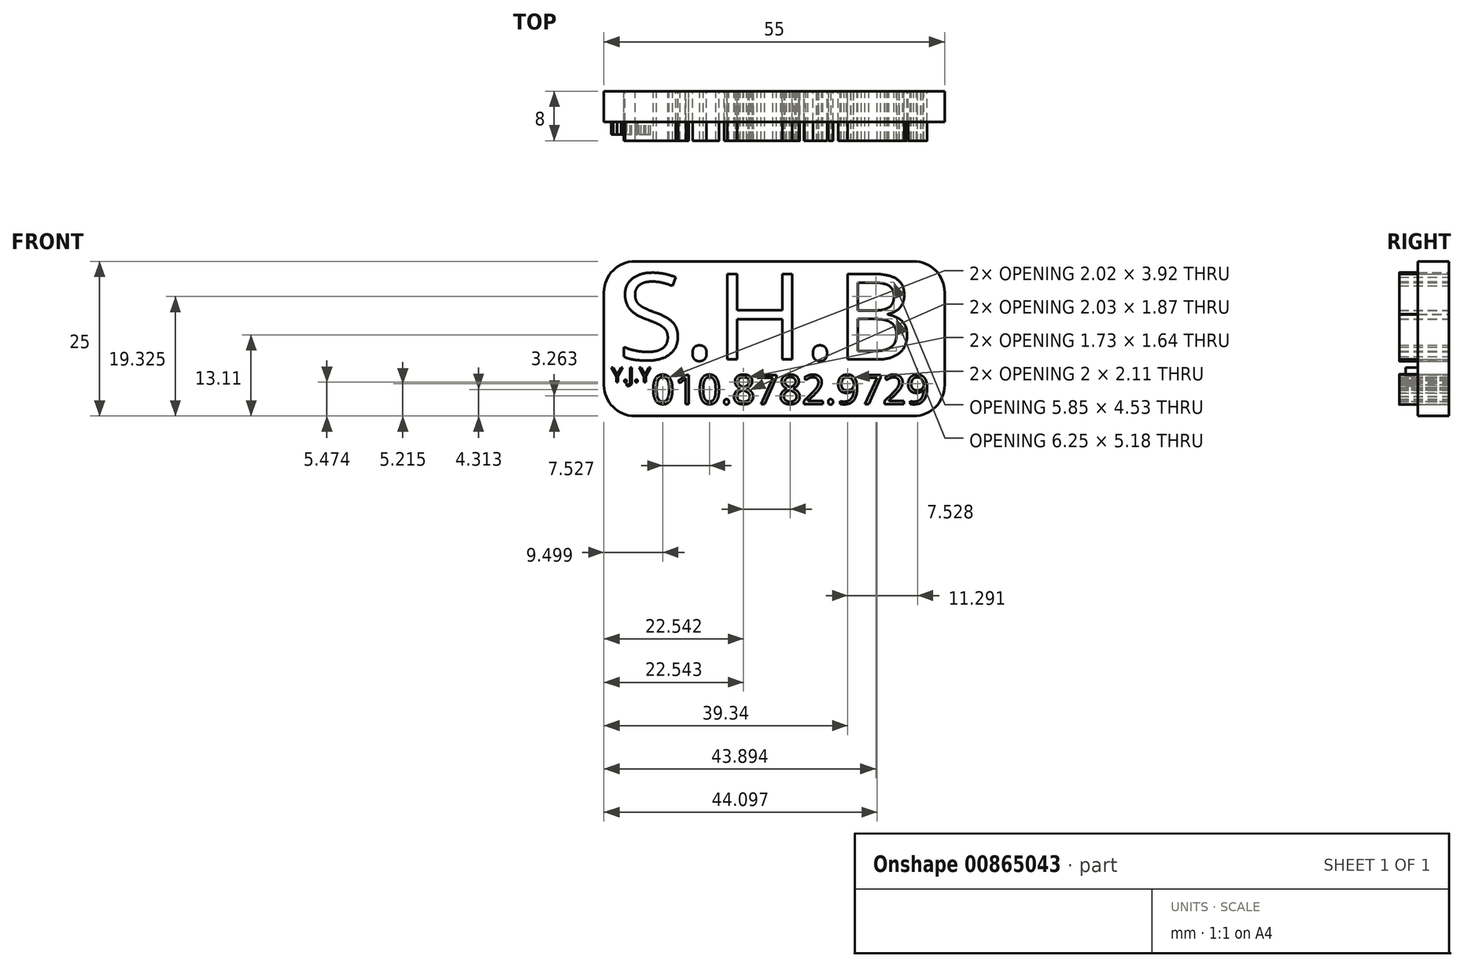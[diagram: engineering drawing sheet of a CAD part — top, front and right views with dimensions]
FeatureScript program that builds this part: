
annotation { "Feature Type Name" : "Feature", "Feature Type Description" : "" }
export const myFeature = defineFeature(function(context is Context, id is Id, definition is map)
    precondition{}
    {
        {
            var Q0;
            Q0=qCreatedBy(makeId("Front.planeOp"),FACE);
            var sketch = newSketch(context, id + "F0", { "sketchPlane" : qUnion([Q0])});
            skLineSegment(sketch, "E0.bottom", {"start": v(0, 0) * mm, "end": v(55, 0) * mm});
            skLineSegment(sketch, "E0.top", {"start": v(0, 25) * mm, "end": v(55, 25) * mm});
            skLineSegment(sketch, "E0.left", {"start": v(0, 0) * mm, "end": v(0, 25) * mm});
            skLineSegment(sketch, "E0.right", {"start": v(55, 0) * mm, "end": v(55, 25) * mm});
            skSolve(sketch);
        }
        {
            var Q0;
            Q0=makeQuery(id+"F0.imprint","IMPRINT",FACE,{"disambiguationData":[TD([[makeQuery(id+"F0.imprint","IMPRINT",EDGE,{"derivedFrom":sQuery(id+"F0.wireOp",EDGE,"E0.bottom")}),1.0]])]});
            var sketch = newSketch(context, id + "F1", { "sketchPlane" : qUnion([Q0])});
            skText(sketch, "E1", { "text": "S.H.B\n", "fontName": "OpenSans-Regular.ttf"});
            skText(sketch, "E2", { "text": "010.8782.9729", "fontName": "OpenSans-Regular.ttf"});
            const initialGuessF1  = {"E1": [0.00222, 0.00915, 1, 0, 0.01395], "E2": [0.00762, 0.00196, 1, 0, 0.00474]};
            skSetInitialGuess(sketch, initialGuessF1);
            skSolve(sketch);
        }
        {
            var Q0;
            Q0 = qSketchRegion(id + "F1", true);
            extrude(context, id + "F2", {"entities" : qUnion([Q0]), "depth" : 8 * mm, "offsetDistance" : 25 * mm});
        }
        {
            var Q0;
            Q0=makeQuery(id+"F0.imprint","IMPRINT",FACE,{"disambiguationData":[TD([[makeQuery(id+"F0.imprint","IMPRINT",EDGE,{"derivedFrom":sQuery(id+"F0.wireOp",EDGE,"E0.bottom")}),1.0]])]});
            extrude(context, id + "F3", {"entities" : qUnion([Q0]), "depth" : 5 * mm, "offsetDistance" : 25 * mm});
        }
        {
            var Q0;
            Q0=makeQuery(id+"F3.opExtrude","SWEPT_EDGE",EDGE,{"disambiguationData":[OSD([sQuery(id+"F0.wireOp",EDGE,"E0.top"),sQuery(id+"F0.wireOp",EDGE,"E0.right")])]});
            var Q1;
            Q1=makeQuery(id+"F3.opExtrude","SWEPT_EDGE",EDGE,{"disambiguationData":[OSD([sQuery(id+"F0.wireOp",EDGE,"E0.top"),sQuery(id+"F0.wireOp",EDGE,"E0.left")])]});
            var Q2;
            Q2=makeQuery(id+"F3.opExtrude","SWEPT_EDGE",EDGE,{"disambiguationData":[OSD([sQuery(id+"F0.wireOp",EDGE,"E0.bottom"),sQuery(id+"F0.wireOp",EDGE,"E0.left")])]});
            var Q3;
            Q3=makeQuery(id+"F3.opExtrude","SWEPT_EDGE",EDGE,{"disambiguationData":[OSD([sQuery(id+"F0.wireOp",EDGE,"E0.bottom"),sQuery(id+"F0.wireOp",EDGE,"E0.right")])]});
            fillet(context, id + "F4", {"entities" : qUnion([Q0, Q1, Q2, Q3]), "radius" : 5 * mm, "tangentPropagation" : true, "allowEdgeOverflow" : false});
        }
        {
            var Q0;
            Q0=makeQuery(id+"F3.opExtrude","CAP_FACE",FACE,{"disambiguationData":[OSD([sQuery(id+"F0.wireOp",EDGE,"E0.bottom"),sQuery(id+"F0.wireOp",EDGE,"E0.top"),sQuery(id+"F0.wireOp",EDGE,"E0.left"),sQuery(id+"F0.wireOp",EDGE,"E0.right")])],"isStart":false});
            var sketch = newSketch(context, id + "F5", { "sketchPlane" : qUnion([Q0])});
            skText(sketch, "E3", { "text": "Y.J.Y", "fontName": "OpenSans-Regular.ttf"});
            const initialGuessF5  = {"E3": [0.00119, 0.0055, 1, 0, 0.00238]};
            skSetInitialGuess(sketch, initialGuessF5);
            skSolve(sketch);
        }
        {
            var Q0;
            Q0 = qSketchRegion(id + "F5", true);
            extrude(context, id + "F6", {"entities" : qUnion([Q0]), "operationType" : NewBodyOperationType.ADD, "depth" : 2 * mm, "offsetDistance" : 25 * mm});
        }
    });
